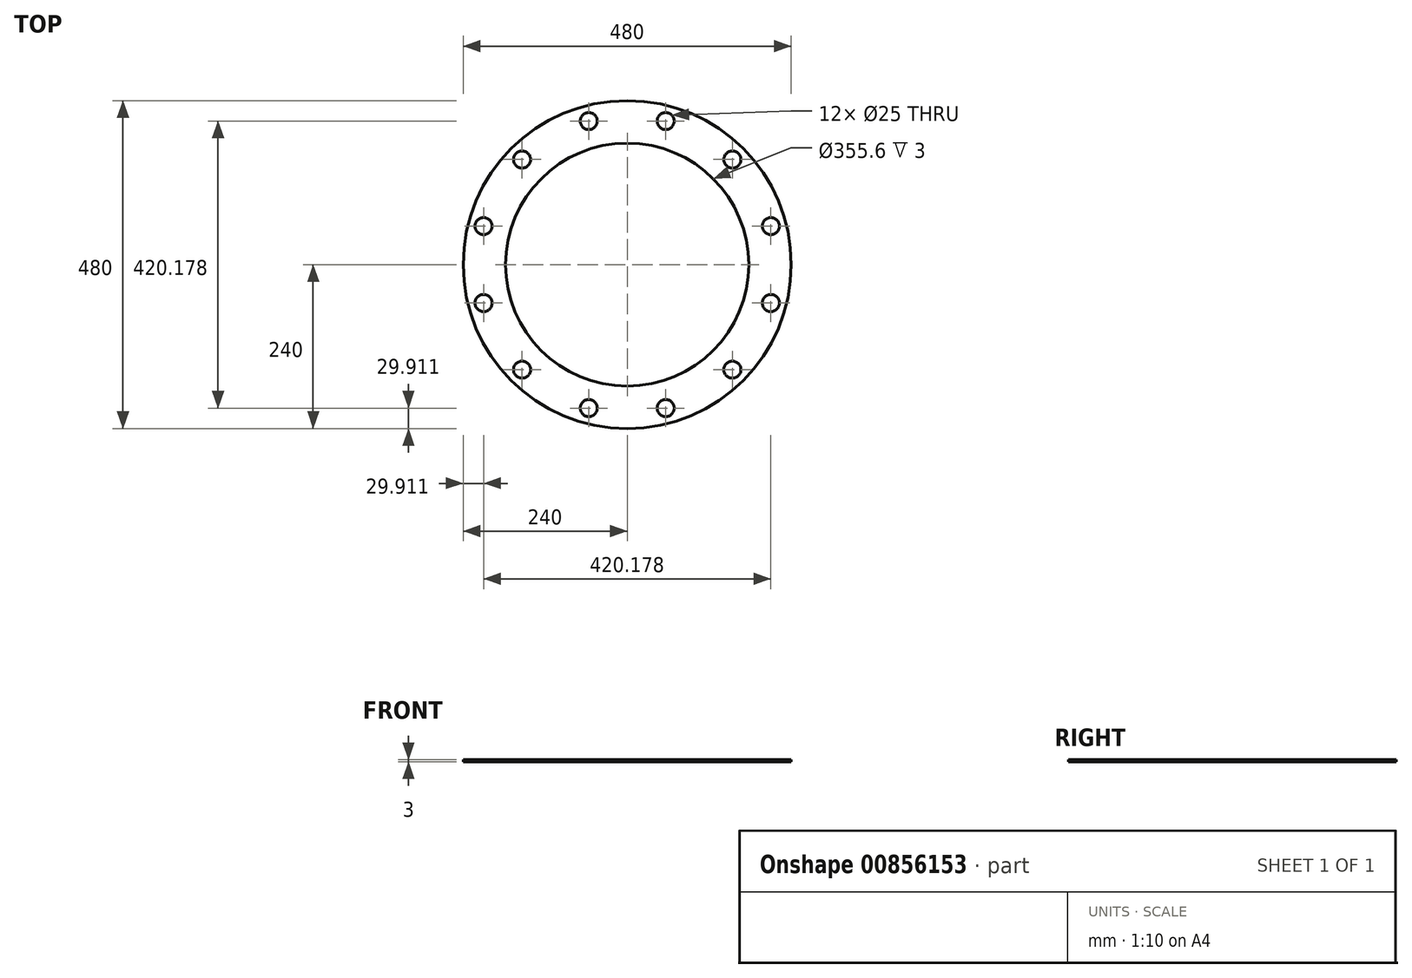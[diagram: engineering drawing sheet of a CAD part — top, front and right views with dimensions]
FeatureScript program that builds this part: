
annotation { "Feature Type Name" : "Feature", "Feature Type Description" : "" }
export const myFeature = defineFeature(function(context is Context, id is Id, definition is map)
    precondition{}
    {
        {
            var Q0;
            Q0=qCreatedBy(makeId("Top.planeOp"),FACE);
            cPlane(context, id + "F0", {"entities" : qUnion([Q0]), "cplaneType" : CPlaneType.OFFSET, "offset" : 512 * mm, "width" : 150 * mm, "height" : 150 * mm});
        }
        {
            var Q0;
            Q0=qCreatedBy(id+"F0.planeOp",FACE);
            var sketch = newSketch(context, id + "F1", { "sketchPlane" : qUnion([Q0])});
            skCircle(sketch, "E0", {"center": v(0, 101.6) * mm, "radius": 240 * mm});
            skLineSegment(sketch, "E1", {"start": v(0, 382.52) * mm, "end": v(0, -185.4) * mm, "construction": true});
            skLineSegment(sketch, "E2", {"start": v(268.79, 101.6) * mm, "end": v(-280.92, 101.6) * mm, "construction": true});
            skCircle(sketch, "E3", {"center": v(0, 101.6) * mm, "radius": 177.8 * mm});
            skCircle(sketch, "E4", {"center": v(0, 101.6) * mm, "radius": 217.5 * mm, "construction": true});
            skCircle(sketch, "E5", {"center": v(210.09, 157.9) * mm, "radius": 12.5 * mm});
            skCircle(sketch, "E6.1.0", {"center": v(153.8, 255.4) * mm, "radius": 12.5 * mm});
            skCircle(sketch, "E6.2.0", {"center": v(56.3, 311.69) * mm, "radius": 12.5 * mm});
            skCircle(sketch, "E6.3.0", {"center": v(-56.3, 311.69) * mm, "radius": 12.5 * mm});
            skCircle(sketch, "E6.4.0", {"center": v(-153.8, 255.4) * mm, "radius": 12.5 * mm});
            skCircle(sketch, "E6.5.0", {"center": v(-210.09, 157.9) * mm, "radius": 12.5 * mm});
            skCircle(sketch, "E6.6.0", {"center": v(-210.09, 45.3) * mm, "radius": 12.5 * mm});
            skCircle(sketch, "E6.7.0", {"center": v(-153.8, -52.2) * mm, "radius": 12.5 * mm});
            skCircle(sketch, "E6.8.0", {"center": v(-56.3, -108.49) * mm, "radius": 12.5 * mm});
            skCircle(sketch, "E6.9.0", {"center": v(56.3, -108.49) * mm, "radius": 12.5 * mm});
            skCircle(sketch, "E6.10.0", {"center": v(153.8, -52.2) * mm, "radius": 12.5 * mm});
            skCircle(sketch, "E6.11.0", {"center": v(210.09, 45.3) * mm, "radius": 12.5 * mm});
            skSolve(sketch);
        }
        {
            var Q0;
            Q0=makeQuery(id+"F1.imprint","IMPRINT",FACE,{"disambiguationData":[TD([[makeQuery(id+"F1.imprint","IMPRINT",EDGE,{"derivedFrom":sQuery(id+"F1.wireOp",EDGE,"E0")}),1.0]])]});
            extrude(context, id + "F2", {"entities" : qUnion([Q0]), "oppositeDirection" : true, "depth" : 3 * mm, "offsetDistance" : 25 * mm});
        }
    });
